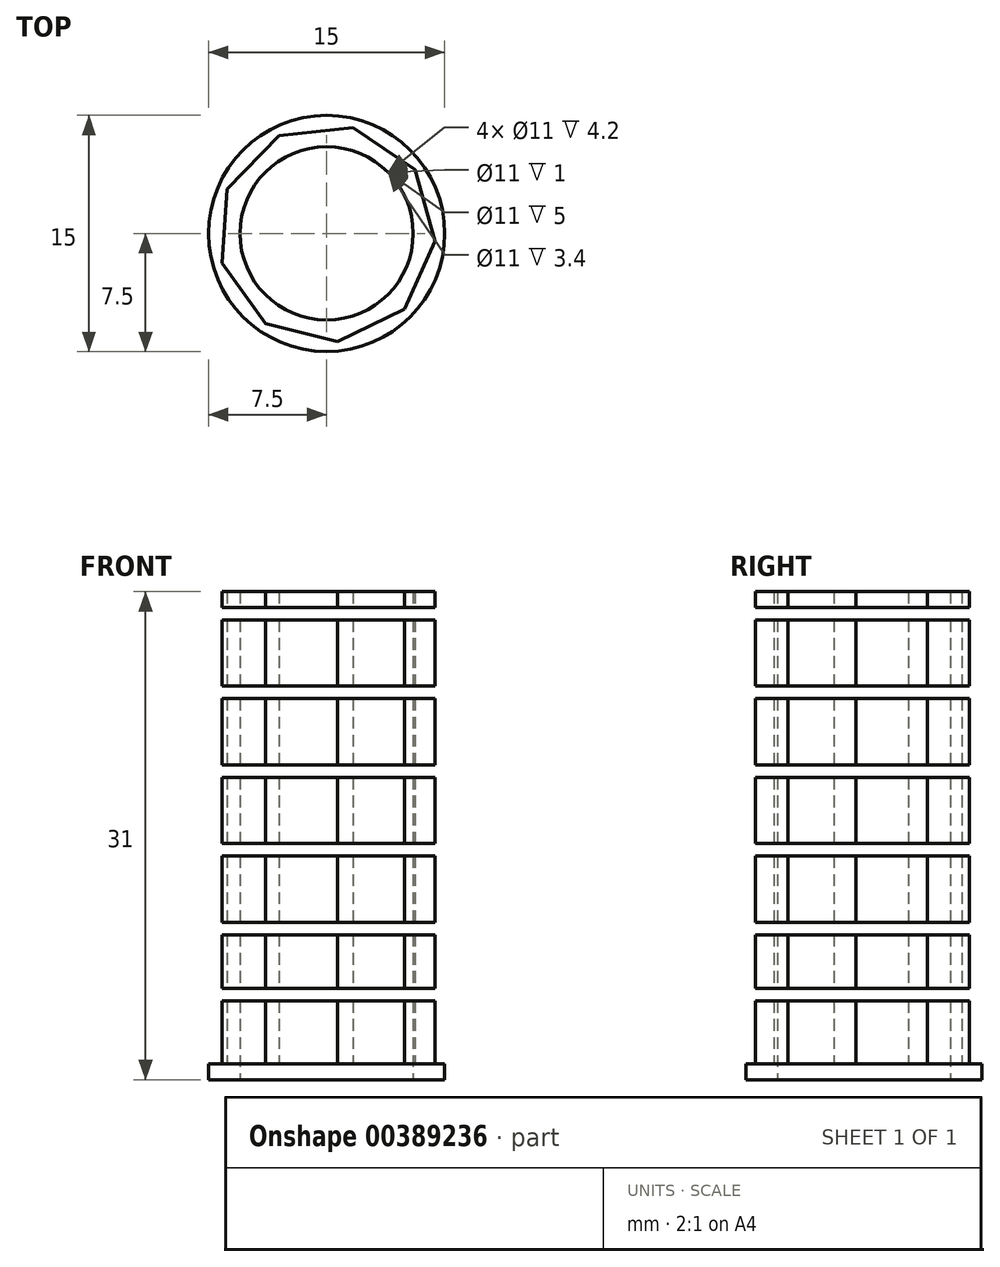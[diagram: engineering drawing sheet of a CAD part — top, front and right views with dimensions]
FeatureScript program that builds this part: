
annotation { "Feature Type Name" : "Feature", "Feature Type Description" : "" }
export const myFeature = defineFeature(function(context is Context, id is Id, definition is map)
    precondition{}
    {
        {
            var Q0;
            Q0=qCreatedBy(makeId("Top.planeOp"),FACE);
            var sketch = newSketch(context, id + "F0", { "sketchPlane" : qUnion([Q0])});
            skCircle(sketch, "E0", {"center": v(0, 0) * mm, "radius": 7.5 * mm});
            skCircle(sketch, "E1.cCircle", {"center": v(0, 0) * mm, "radius": 6.5 * mm, "construction": true});
            skLineSegment(sketch, "E1.0", {"start": v(-6.31, 2.83) * mm, "end": v(-3.02, 6.23) * mm});
            skLineSegment(sketch, "E1.1", {"start": v(-3.02, 6.23) * mm, "end": v(1.7, 6.7) * mm});
            skLineSegment(sketch, "E1.2", {"start": v(1.7, 6.7) * mm, "end": v(5.6, 4.05) * mm});
            skLineSegment(sketch, "E1.3", {"start": v(5.6, 4.05) * mm, "end": v(6.9, -0.5) * mm});
            skLineSegment(sketch, "E1.4", {"start": v(6.9, -0.5) * mm, "end": v(4.96, -4.82) * mm});
            skLineSegment(sketch, "E1.5", {"start": v(4.96, -4.82) * mm, "end": v(0.7, -6.88) * mm});
            skLineSegment(sketch, "E1.6", {"start": v(0.7, -6.88) * mm, "end": v(-3.88, -5.72) * mm});
            skLineSegment(sketch, "E1.7", {"start": v(-3.88, -5.72) * mm, "end": v(-6.65, -1.89) * mm});
            skLineSegment(sketch, "E1.8", {"start": v(-6.65, -1.89) * mm, "end": v(-6.31, 2.83) * mm});
            skPoint(sketch, "E1.0.midPoint", {"position": v(-4.66, 4.53) * mm});
            skCircle(sketch, "E2", {"center": v(0, 0) * mm, "radius": 5.5 * mm});
            skSolve(sketch);
        }
        {
            var Q0;
            Q0 = qSketchRegion(id + "F0", true);
            var Q1;
            Q1=makeQuery(id+"F0.imprint","IMPRINT",FACE,{"disambiguationData":[TD([[makeQuery(id+"F0.imprint","IMPRINT",EDGE,{"derivedFrom":sQuery(id+"F0.wireOp",EDGE,"E1.0")}),-1.0]])]});
            extrude(context, id + "F1", {"entities" : qUnion([Q0, Q1]), "depth" : 1 * mm, "offsetDistance" : 25 * mm});
        }
        {
            var Q0;
            Q0=makeQuery(id+"F0.imprint","IMPRINT",FACE,{"disambiguationData":[TD([[makeQuery(id+"F0.imprint","IMPRINT",EDGE,{"derivedFrom":sQuery(id+"F0.wireOp",EDGE,"E1.0")}),-1.0]])]});
            extrude(context, id + "F2", {"entities" : qUnion([Q0]), "operationType" : NewBodyOperationType.ADD, "depth" : 31 * mm, "offsetDistance" : 25 * mm});
        }
        {
            var Q0;
            Q0=qCreatedBy(makeId("Top.planeOp"),FACE);
            cPlane(context, id + "F3", {"entities" : qUnion([Q0]), "cplaneType" : CPlaneType.OFFSET, "offset" : 5 * mm, "width" : 150 * mm, "height" : 150 * mm});
        }
        {
            var Q0;
            Q0=qCreatedBy(id+"F3.planeOp",FACE);
            var sketch = newSketch(context, id + "F4", { "sketchPlane" : qUnion([Q0])});
            skCircle(sketch, "E3", {"center": v(0, 0) * mm, "radius": 2.45 * mm});
            skCircle(sketch, "E4", {"center": v(0, 0) * mm, "radius": 15 * mm});
            skSolve(sketch);
        }
        {
            var Q0;
            Q0 = qSketchRegion(id + "F4", true);
            extrude(context, id + "F5", {"entities" : qUnion([Q0]), "operationType" : NewBodyOperationType.REMOVE, "depth" : 0.8 * mm, "offsetDistance" : 25 * mm});
        }
        {
            var Q0;
            Q0=qCreatedBy(makeId("Top.planeOp"),FACE);
            cPlane(context, id + "F6", {"entities" : qUnion([Q0]), "cplaneType" : CPlaneType.OFFSET, "offset" : 10 * mm, "width" : 150 * mm, "height" : 150 * mm});
        }
        {
            var Q0;
            Q0=qCreatedBy(id+"F6.planeOp",FACE);
            var sketch = newSketch(context, id + "F7", { "sketchPlane" : qUnion([Q0])});
            skCircle(sketch, "E5", {"center": v(0, 0) * mm, "radius": 2.45 * mm});
            skCircle(sketch, "E6", {"center": v(0, 0) * mm, "radius": 15 * mm});
            skSolve(sketch);
        }
        {
            var Q0;
            Q0=makeQuery(id+"F7.imprint","IMPRINT",FACE,{"disambiguationData":[TD([[makeQuery(id+"F7.imprint","IMPRINT",EDGE,{"derivedFrom":sQuery(id+"F7.wireOp",EDGE,"E5")}),-1.0]])]});
            extrude(context, id + "F8", {"entities" : qUnion([Q0]), "operationType" : NewBodyOperationType.REMOVE, "oppositeDirection" : true, "depth" : 0.8 * mm, "offsetDistance" : 25 * mm});
        }
        {
            var Q0;
            Q0=qCreatedBy(id+"F6.planeOp",FACE);
            cPlane(context, id + "F9", {"entities" : qUnion([Q0]), "cplaneType" : CPlaneType.OFFSET, "offset" : 5 * mm, "width" : 150 * mm, "height" : 150 * mm});
        }
        {
            var Q0;
            Q0=qCreatedBy(id+"F9.planeOp",FACE);
            var sketch = newSketch(context, id + "F10", { "sketchPlane" : qUnion([Q0])});
            skCircle(sketch, "E7", {"center": v(0, 0) * mm, "radius": 2.45 * mm});
            skCircle(sketch, "E8", {"center": v(0, 0) * mm, "radius": 15 * mm});
            skSolve(sketch);
        }
        {
            var Q0;
            Q0=makeQuery(id+"F10.imprint","IMPRINT",FACE,{"disambiguationData":[TD([[makeQuery(id+"F10.imprint","IMPRINT",EDGE,{"derivedFrom":sQuery(id+"F10.wireOp",EDGE,"E7")}),-1.0]])]});
            extrude(context, id + "F11", {"entities" : qUnion([Q0]), "operationType" : NewBodyOperationType.REMOVE, "oppositeDirection" : true, "depth" : 0.8 * mm, "offsetDistance" : 25 * mm});
        }
        {
            var Q0;
            Q0=qCreatedBy(id+"F9.planeOp",FACE);
            cPlane(context, id + "F12", {"entities" : qUnion([Q0]), "cplaneType" : CPlaneType.OFFSET, "offset" : 5 * mm, "width" : 150 * mm, "height" : 150 * mm});
        }
        {
            var Q0;
            Q0=qCreatedBy(id+"F12.planeOp",FACE);
            var sketch = newSketch(context, id + "F13", { "sketchPlane" : qUnion([Q0])});
            skCircle(sketch, "E9", {"center": v(0, 0) * mm, "radius": 2.45 * mm});
            skCircle(sketch, "E10", {"center": v(0, 0) * mm, "radius": 15 * mm});
            skSolve(sketch);
        }
        {
            var Q0;
            Q0 = qSketchRegion(id + "F13", true);
            extrude(context, id + "F14", {"entities" : qUnion([Q0]), "operationType" : NewBodyOperationType.REMOVE, "oppositeDirection" : true, "depth" : 0.8 * mm, "offsetDistance" : 25 * mm});
        }
        {
            var Q0;
            Q0=qCreatedBy(id+"F12.planeOp",FACE);
            cPlane(context, id + "F15", {"entities" : qUnion([Q0]), "cplaneType" : CPlaneType.OFFSET, "offset" : 5 * mm, "width" : 150 * mm, "height" : 150 * mm});
        }
        {
            var Q0;
            Q0=qCreatedBy(id+"F15.planeOp",FACE);
            var sketch = newSketch(context, id + "F16", { "sketchPlane" : qUnion([Q0])});
            skCircle(sketch, "E11", {"center": v(0, 0) * mm, "radius": 2.45 * mm});
            skCircle(sketch, "E12", {"center": v(0, 0) * mm, "radius": 15 * mm});
            skSolve(sketch);
        }
        {
            var Q0;
            Q0=makeQuery(id+"F16.imprint","IMPRINT",FACE,{"disambiguationData":[TD([[makeQuery(id+"F16.imprint","IMPRINT",EDGE,{"derivedFrom":sQuery(id+"F16.wireOp",EDGE,"E11")}),-1.0]])]});
            extrude(context, id + "F17", {"entities" : qUnion([Q0]), "operationType" : NewBodyOperationType.REMOVE, "oppositeDirection" : true, "depth" : 0.8 * mm, "offsetDistance" : 25 * mm});
        }
        {
            var Q0;
            Q0=qCreatedBy(id+"F15.planeOp",FACE);
            cPlane(context, id + "F18", {"entities" : qUnion([Q0]), "cplaneType" : CPlaneType.OFFSET, "offset" : 5 * mm, "width" : 150 * mm, "height" : 150 * mm});
        }
        {
            var Q0;
            Q0=qCreatedBy(id+"F18.planeOp",FACE);
            var sketch = newSketch(context, id + "F19", { "sketchPlane" : qUnion([Q0])});
            skCircle(sketch, "E13", {"center": v(0, 0) * mm, "radius": 2.45 * mm});
            skCircle(sketch, "E14", {"center": v(0, 0) * mm, "radius": 15 * mm});
            skSolve(sketch);
        }
        {
            var Q0;
            Q0=makeQuery(id+"F19.imprint","IMPRINT",FACE,{"disambiguationData":[TD([[makeQuery(id+"F19.imprint","IMPRINT",EDGE,{"derivedFrom":sQuery(id+"F19.wireOp",EDGE,"E13")}),-1.0]])]});
            extrude(context, id + "F20", {"entities" : qUnion([Q0]), "operationType" : NewBodyOperationType.REMOVE, "oppositeDirection" : true, "depth" : 0.8 * mm, "offsetDistance" : 25 * mm});
        }
        {
            var Q0;
            Q0=qCreatedBy(id+"F18.planeOp",FACE);
            cPlane(context, id + "F21", {"entities" : qUnion([Q0]), "cplaneType" : CPlaneType.OFFSET, "offset" : 5 * mm, "width" : 150 * mm, "height" : 150 * mm});
        }
        {
            var Q0;
            Q0=qCreatedBy(id+"F21.planeOp",FACE);
            var sketch = newSketch(context, id + "F22", { "sketchPlane" : qUnion([Q0])});
            skCircle(sketch, "E15", {"center": v(0, 0) * mm, "radius": 2.45 * mm});
            skCircle(sketch, "E16", {"center": v(0, 0) * mm, "radius": 15 * mm});
            skSolve(sketch);
        }
        {
            var Q0;
            Q0=makeQuery(id+"F22.imprint","IMPRINT",FACE,{"disambiguationData":[TD([[makeQuery(id+"F22.imprint","IMPRINT",EDGE,{"derivedFrom":sQuery(id+"F22.wireOp",EDGE,"E15")}),-1.0]])]});
            extrude(context, id + "F23", {"entities" : qUnion([Q0]), "operationType" : NewBodyOperationType.REMOVE, "oppositeDirection" : true, "depth" : 0.8 * mm, "offsetDistance" : 25 * mm});
        }
    });
